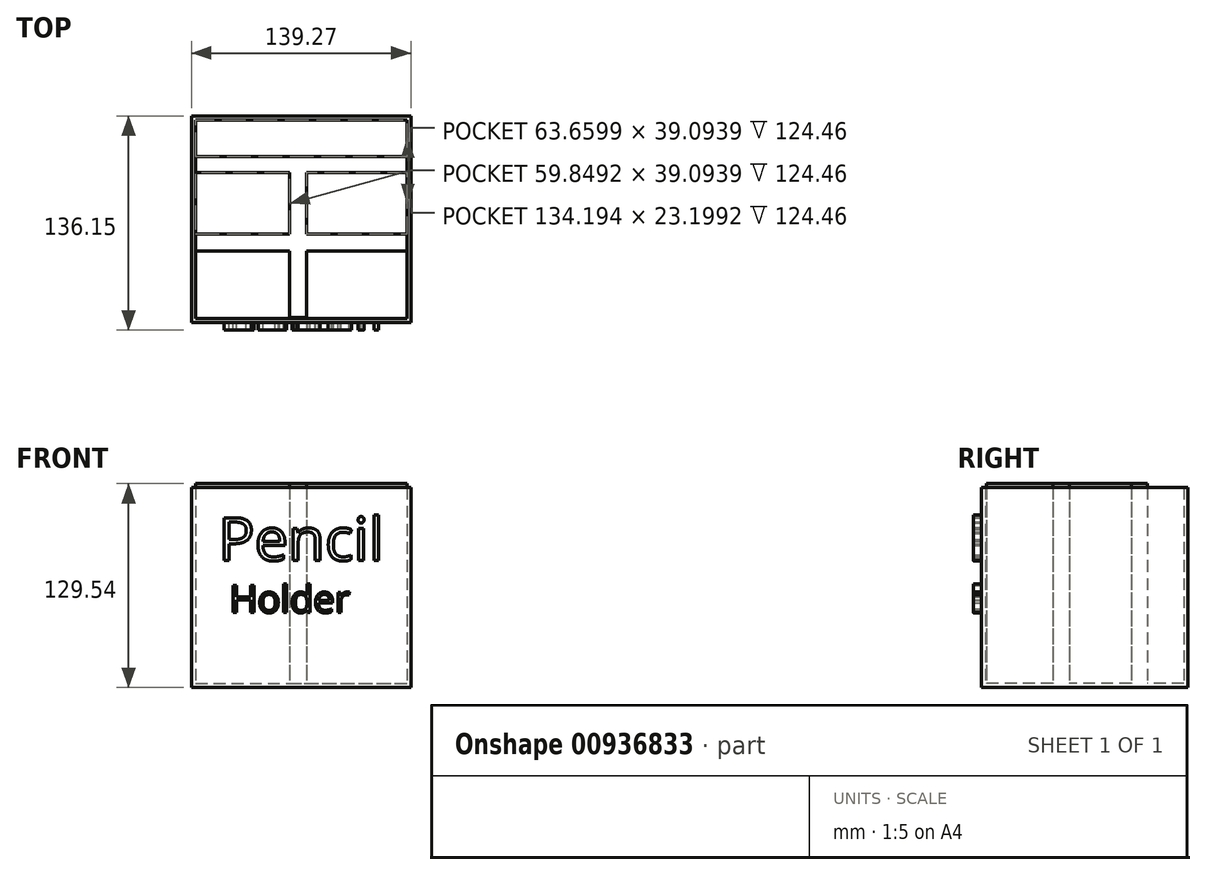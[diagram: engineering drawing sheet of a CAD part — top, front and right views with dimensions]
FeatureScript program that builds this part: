
annotation { "Feature Type Name" : "Feature", "Feature Type Description" : "" }
export const myFeature = defineFeature(function(context is Context, id is Id, definition is map)
    precondition{}
    {
        {
            var Q0;
            Q0=qCreatedBy(makeId("Top.planeOp"),FACE);
            var sketch = newSketch(context, id + "F0", { "sketchPlane" : qUnion([Q0])});
            skLineSegment(sketch, "E0.bottom", {"start": v(-71.21, 65.99) * mm, "end": v(68.06, 65.99) * mm});
            skLineSegment(sketch, "E0.top", {"start": v(-71.21, -65.16) * mm, "end": v(68.06, -65.16) * mm});
            skLineSegment(sketch, "E0.left", {"start": v(-71.21, 65.99) * mm, "end": v(-71.21, -65.16) * mm});
            skLineSegment(sketch, "E0.right", {"start": v(68.06, 65.99) * mm, "end": v(68.06, -65.16) * mm});
            skSolve(sketch);
        }
        {
            var Q0;
            Q0=makeQuery(id+"F0.imprint","IMPRINT",FACE,{"disambiguationData":[TD([[makeQuery(id+"F0.imprint","IMPRINT",EDGE,{"derivedFrom":sQuery(id+"F0.wireOp",EDGE,"E0.bottom")}),-1.0]])]});
            extrude(context, id + "F1", {"entities" : qUnion([Q0]), "depth" : 127 * mm, "offsetDistance" : 25.4 * mm});
        }
        {
            var Q0;
            Q0=makeQuery(id+"F1.opExtrude","CAP_FACE",FACE,{"disambiguationData":[OSD([sQuery(id+"F0.wireOp",EDGE,"E0.bottom"),sQuery(id+"F0.wireOp",EDGE,"E0.top"),sQuery(id+"F0.wireOp",EDGE,"E0.left"),sQuery(id+"F0.wireOp",EDGE,"E0.right")])],"isStart":false});
            shell(context, id + "F2", {"entities" : qUnion([Q0]), "thickness" : 2.54 * mm});
        }
        {
            var Q0;
            Q0=makeQuery(id+"F1.opExtrude","SWEPT_FACE",FACE,{"disambiguationData":[OSD([sQuery(id+"F0.wireOp",EDGE,"E0.top")])]});
            var sketch = newSketch(context, id + "F3", { "sketchPlane" : qUnion([Q0])});
            skText(sketch, "E1", { "text": "Pencil ", "fontName": "OpenSans-Regular.ttf"});
            const initialGuessF3  = {"E1": [-0.05416, 0.08072, 1, 0, 0.02742]};
            skSetInitialGuess(sketch, initialGuessF3);
            skSolve(sketch);
        }
        {
            var Q0;
            Q0 = qSketchRegion(id + "F3", true);
            extrude(context, id + "F4", {"entities" : qUnion([Q0]), "operationType" : NewBodyOperationType.ADD, "depth" : 5 * mm, "offsetDistance" : 25.4 * mm});
        }
        {
            var Q0;
            {var subQ1=sQuery(id+"F0.wireOp",EDGE,"E0.left");var subQ2=sQuery(id+"F0.wireOp",EDGE,"E0.top");Q0=makeQuery(id+"F4.boolean.opBoolean","SPLIT",FACE,{"disambiguationData":[TD([makeQuery(id+"F1.opExtrude","SWEPT_FACE",FACE,{"disambiguationData":[OSD([subQ1])]})])],"derivedFrom":makeQuery(id+"F1.opExtrude","SWEPT_FACE",FACE,{"disambiguationData":[OSD([subQ2])]})});}
            var sketch = newSketch(context, id + "F5", { "sketchPlane" : qUnion([Q0])});
            skText(sketch, "E2", { "text": "Holder", "fontName": "OpenSans-Regular.ttf"});
            const initialGuessF5  = {"E2": [-0.04705, 0.04766, 1, 0, 0.01734]};
            skSetInitialGuess(sketch, initialGuessF5);
            skSolve(sketch);
        }
        {
            var Q0;
            Q0 = qSketchRegion(id + "F5", true);
            extrude(context, id + "F6", {"entities" : qUnion([Q0]), "operationType" : NewBodyOperationType.ADD, "depth" : 5 * mm, "offsetDistance" : 25.4 * mm});
        }
        {
            var Q0;
            Q0=makeQuery(id+"F2.opShell","OFFSET_FACE",FACE,{"disambiguationData":[OSD([sQuery(id+"F0.wireOp",EDGE,"E0.bottom"),sQuery(id+"F0.wireOp",EDGE,"E0.top"),sQuery(id+"F0.wireOp",EDGE,"E0.left"),sQuery(id+"F0.wireOp",EDGE,"E0.right")])]});
            var sketch = newSketch(context, id + "F7", { "sketchPlane" : qUnion([Q0])});
            skLineSegment(sketch, "E3.bottom", {"start": v(-68.67, 40.25) * mm, "end": v(65.52, 40.25) * mm});
            skLineSegment(sketch, "E3.top", {"start": v(-68.67, 29.98) * mm, "end": v(65.52, 29.98) * mm});
            skLineSegment(sketch, "E3.left", {"start": v(-68.67, 40.25) * mm, "end": v(-68.67, 29.98) * mm});
            skLineSegment(sketch, "E3.right", {"start": v(65.52, 40.25) * mm, "end": v(65.52, 29.98) * mm});
            skSolve(sketch);
        }
        {
            var Q0;
            Q0 = qSketchRegion(id + "F7", true);
            extrude(context, id + "F8", {"entities" : qUnion([Q0]), "operationType" : NewBodyOperationType.ADD, "depth" : 127 * mm, "offsetDistance" : 25.4 * mm});
        }
        {
            var Q0;
            {var subQ0=sQuery(id+"F0.wireOp",EDGE,"E0.top");var subQ1=sQuery(id+"F0.wireOp",EDGE,"E0.left");var subQ2=sQuery(id+"F0.wireOp",EDGE,"E0.right");Q0=makeQuery(id+"F8.boolean.opBoolean","SPLIT",FACE,{"disambiguationData":[TD([makeQuery(id+"F2.opShell","OFFSET_FACE",FACE,{"disambiguationData":[OSD([subQ0])]})])],"derivedFrom":makeQuery(id+"F2.opShell","OFFSET_FACE",FACE,{"disambiguationData":[OSD([sQuery(id+"F0.wireOp",EDGE,"E0.bottom"),subQ0,subQ1,subQ2])]})});}
            var sketch = newSketch(context, id + "F9", { "sketchPlane" : qUnion([Q0])});
            skLineSegment(sketch, "E4.bottom", {"start": v(-68.67, -9.11) * mm, "end": v(65.52, -9.11) * mm});
            skLineSegment(sketch, "E4.top", {"start": v(-68.67, -19.72) * mm, "end": v(65.52, -19.72) * mm});
            skLineSegment(sketch, "E4.left", {"start": v(-68.67, -9.11) * mm, "end": v(-68.67, -19.72) * mm});
            skLineSegment(sketch, "E4.right", {"start": v(65.52, -9.11) * mm, "end": v(65.52, -19.72) * mm});
            skSolve(sketch);
        }
        {
            var Q0;
            Q0=makeQuery(id+"F9.imprint","IMPRINT",FACE,{"disambiguationData":[TD([[makeQuery(id+"F9.imprint","IMPRINT",EDGE,{"derivedFrom":sQuery(id+"F9.wireOp",EDGE,"E4.bottom")}),-1.0]])]});
            extrude(context, id + "F10", {"entities" : qUnion([Q0]), "operationType" : NewBodyOperationType.ADD, "depth" : 127 * mm, "offsetDistance" : 25.4 * mm});
        }
        {
            var Q0;
            {var subQ0=sQuery(id+"F0.wireOp",EDGE,"E0.bottom");var subQ1=sQuery(id+"F0.wireOp",EDGE,"E0.left");var subQ2=sQuery(id+"F0.wireOp",EDGE,"E0.right");Q0=makeQuery(id+"F8.boolean.opBoolean","SPLIT",FACE,{"disambiguationData":[TD([makeQuery(id+"F2.opShell","OFFSET_FACE",FACE,{"disambiguationData":[OSD([subQ0])]})])],"derivedFrom":makeQuery(id+"F2.opShell","OFFSET_FACE",FACE,{"disambiguationData":[OSD([subQ0,sQuery(id+"F0.wireOp",EDGE,"E0.top"),subQ1,subQ2])]})});}
            var sketch = newSketch(context, id + "F11", { "sketchPlane" : qUnion([Q0])});
            skLineSegment(sketch, "E5.bottom", {"start": v(-8.82, 63.45) * mm, "end": v(1.86, 63.45) * mm});
            skLineSegment(sketch, "E5.top", {"start": v(-8.82, -62) * mm, "end": v(1.86, -62) * mm});
            skLineSegment(sketch, "E5.left", {"start": v(-8.82, 63.45) * mm, "end": v(-8.82, -62) * mm});
            skLineSegment(sketch, "E5.right", {"start": v(1.86, 63.45) * mm, "end": v(1.86, -62) * mm});
            skSolve(sketch);
        }
        {
            var Q0;
            {var subQ0=sQuery(id+"F11.wireOp",EDGE,"E5.top");Q0=makeQuery(id+"F11.imprint","IMPRINT",FACE,{"disambiguationData":[TD([[makeQuery(id+"F11.imprint","IMPRINT",EDGE,{"derivedFrom":subQ0}),1.0]])]});}
            extrude(context, id + "F12", {"entities" : qUnion([Q0]), "operationType" : NewBodyOperationType.ADD, "depth" : 127 * mm, "offsetDistance" : 25.4 * mm});
        }
    });
